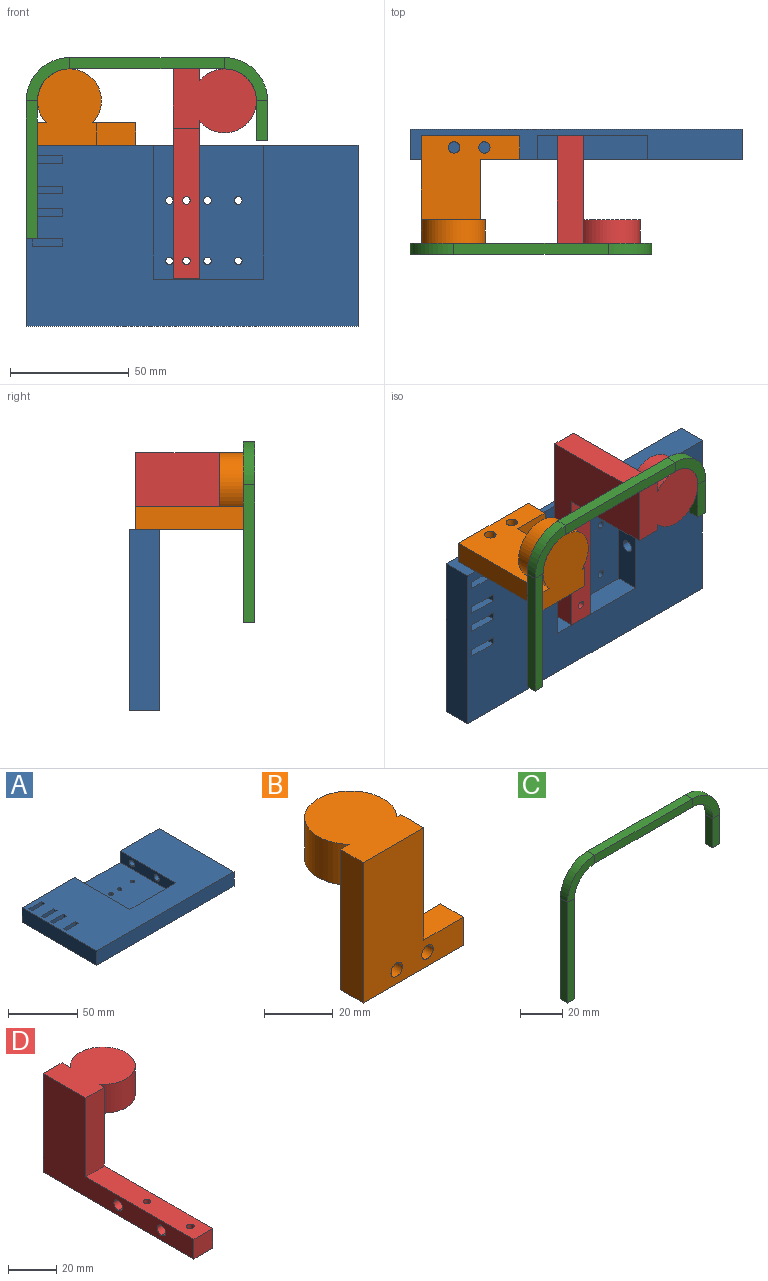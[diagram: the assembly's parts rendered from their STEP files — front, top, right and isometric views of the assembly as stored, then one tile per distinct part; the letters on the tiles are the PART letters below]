
ASSEMBLY  parts=4 mates=9
PART A: 62 faces, bbox 139.7x76.2x12.7 mm
  f0: plane 4.76x4.76mm, normal (0,1,0), area 17.8mm2, adj f1,f2
  f1: cylinder r=2.38mm len=6.35mm, axis (0,1,0), area 47.5mm2, adj f0,f2,f59
  f2: cylinder r=2.38mm len=6.35mm, axis (0,1,0), area 47.5mm2, adj f0,f1,f59
  f3: plane 4.76x4.76mm, normal (0,1,0), area 17.8mm2, adj f4,f5
  f4: cylinder r=2.38mm len=6.35mm, axis (0,1,0), area 47.5mm2, adj f3,f5,f59
  f5: cylinder r=2.38mm len=6.35mm, axis (0,1,0), area 47.5mm2, adj f3,f4,f59
  f6: cylinder r=1.59mm len=3.18mm, axis (0,0,1), area 13.3mm2, adj f7,f58,f61
  f7: cylinder r=1.59mm len=3.18mm, axis (0,0,1), area 13.3mm2, adj f6,f58,f61
  f8: cylinder r=1.59mm len=3.18mm, axis (0,0,1), area 13.3mm2, adj f9,f58,f61
  f9: cylinder r=1.59mm len=3.18mm, axis (0,0,1), area 13.3mm2, adj f8,f58,f61
  f10: cylinder r=1.59mm len=3.18mm, axis (0,0,1), area 13.3mm2, adj f11,f58,f61
  f11: cylinder r=1.59mm len=3.18mm, axis (0,0,1), area 13.3mm2, adj f10,f58,f61
  f12: cylinder r=1.59mm len=3.18mm, axis (0,0,1), area 13.3mm2, adj f13,f58,f61
  f13: cylinder r=1.59mm len=3.18mm, axis (0,0,1), area 13.3mm2, adj f12,f58,f61
  f14: cylinder r=1.59mm len=3.18mm, axis (0,0,1), area 13.3mm2, adj f15,f58,f61
  f15: cylinder r=1.59mm len=3.18mm, axis (0,0,1), area 13.3mm2, adj f14,f58,f61
  f16: cylinder r=1.59mm len=3.18mm, axis (0,0,1), area 13.3mm2, adj f17,f58,f61
  f17: cylinder r=1.59mm len=3.18mm, axis (0,0,1), area 13.3mm2, adj f16,f58,f61
  f18: cylinder r=1.59mm len=3.18mm, axis (0,0,1), area 13.3mm2, adj f19,f58,f61
  f19: cylinder r=1.59mm len=3.18mm, axis (0,0,1), area 13.3mm2, adj f18,f58,f61
  f20: cylinder r=1.59mm len=3.18mm, axis (0,0,1), area 13.3mm2, adj f21,f58,f61
  f21: cylinder r=1.59mm len=3.18mm, axis (0,0,1), area 13.3mm2, adj f20,f58,f61
  f22: plane 12.7x3.23mm, normal (0,0,1), area 41mm2, adj f23,f24,f25,f26
  f23: plane 12.7x10.03mm, normal (0,1,0), area 127.4mm2, adj f22,f24,f26,f56
  f24: plane 10.03x3.23mm, normal (-1,0,0), area 32.4mm2, adj f22,f23,f25,f56
  f25: plane 12.7x10.03mm, normal (0,-1,0), area 127.4mm2, adj f22,f24,f26,f56
  f26: plane 10.03x3.23mm, normal (1,0,0), area 32.4mm2, adj f22,f23,f25,f56
  f27: plane 12.7x3.23mm, normal (0,0,1), area 41mm2, adj f28,f29,f30,f31
  f28: plane 12.7x10.03mm, normal (0,1,0), area 127.4mm2, adj f27,f29,f31,f56
  f29: plane 10.03x3.23mm, normal (-1,0,0), area 32.4mm2, adj f27,f28,f30,f56
  f30: plane 12.7x10.03mm, normal (0,-1,0), area 127.4mm2, adj f27,f29,f31,f56
  f31: plane 10.03x3.23mm, normal (1,0,0), area 32.4mm2, adj f27,f28,f30,f56
  f32: plane 12.7x3.23mm, normal (0,0,1), area 41mm2, adj f33,f34,f35,f36
  f33: plane 12.7x10.03mm, normal (0,1,0), area 127.4mm2, adj f32,f34,f36,f56
  f34: plane 10.03x3.23mm, normal (-1,0,0), area 32.4mm2, adj f32,f33,f35,f56
  f35: plane 12.7x10.03mm, normal (0,-1,0), area 127.4mm2, adj f32,f34,f36,f56
  f36: plane 10.03x3.23mm, normal (1,0,0), area 32.4mm2, adj f32,f33,f35,f56
  f37: plane 12.7x3.23mm, normal (0,0,1), area 41mm2, adj f38,f39,f40,f41
  f38: plane 12.7x10.03mm, normal (0,1,0), area 127.4mm2, adj f37,f39,f41,f56
  f39: plane 10.03x3.23mm, normal (-1,0,0), area 32.4mm2, adj f37,f38,f40,f56
  f40: plane 12.7x10.03mm, normal (0,-1,0), area 127.4mm2, adj f37,f39,f41,f56
  f41: plane 10.03x3.23mm, normal (1,0,0), area 32.4mm2, adj f37,f38,f40,f56
  f42: cylinder r=2.54mm len=39.62mm, axis (1,0,0), area 316.2mm2, adj f43,f47,f57
  f43: cylinder r=2.54mm len=39.62mm, axis (1,0,0), area 316.2mm2, adj f42,f47,f57
  f44: cylinder r=2.54mm len=39.62mm, axis (1,0,0), area 316.2mm2, adj f45,f47,f57
  f45: cylinder r=2.54mm len=39.62mm, axis (1,0,0), area 316.2mm2, adj f44,f47,f57
  f46: plane 139.7x12.7mm, normal (0,-1,0), area 1774.2mm2, adj f47,f56,f60,f61
  f47: plane 76.2x12.7mm, normal (1,0,0), area 927.2mm2, adj f42,f43,f44,f45,f46,f56,f59,f61
  f48: plane 5.08x5.08mm, normal (1,0,0), area 20.3mm2, adj f49,f50
  f49: cylinder r=2.54mm len=15.49mm, axis (1,0,0), area 123.6mm2, adj f48,f50,f55
  f50: cylinder r=2.54mm len=15.49mm, axis (1,0,0), area 123.6mm2, adj f48,f49,f55
  f51: plane 5.08x5.08mm, normal (1,0,0), area 20.3mm2, adj f52,f53
  f52: cylinder r=2.54mm len=15.49mm, axis (1,0,0), area 123.6mm2, adj f51,f53,f55
  f53: cylinder r=2.54mm len=15.49mm, axis (1,0,0), area 123.6mm2, adj f51,f52,f55
  f54: plane 46.48x10.03mm, normal (0,1,0), area 466.4mm2, adj f55,f56,f57,f58
  f55: plane 56.32x10.03mm, normal (1,0,0), area 524.6mm2, adj f49,f50,f52,f53,f54,f56,f58,f59
  f56: plane 139.7x76.2mm, normal (0,0,1), area 7863.2mm2, adj f23,f24,f25,f26,f28,f29,f30,f31
  f57: plane 56.32x10.03mm, normal (-1,0,0), area 524.6mm2, adj f42,f43,f44,f45,f54,f56,f58,f59
  f58: plane 56.32x46.48mm, normal (0,0,1), area 2554.7mm2, adj f6,f7,f8,f9,f10,f11,f12,f13
  f59: plane 139.7x12.7mm, normal (0,1,0), area 1272.2mm2, adj f1,f2,f4,f5,f47,f55,f56,f57
  f60: plane 76.2x12.7mm, normal (-1,0,0), area 967.7mm2, adj f46,f56,f59,f61
  f61: plane 139.7x76.2mm, normal (0,0,-1), area 10581.8mm2, adj f6,f7,f8,f9,f10,f11,f12,f13
PART B: 14 faces, bbox 41.3x32.2x50.1 mm
  f0: cylinder r=2.38mm len=9.46mm, axis (0,-1,0), area 70.8mm2, adj f1,f9,f11
  f1: cylinder r=2.38mm len=9.46mm, axis (0,-1,0), area 70.8mm2, adj f0,f9,f11
  f2: cylinder r=2.38mm len=9.46mm, axis (0,-1,0), area 70.8mm2, adj f3,f9,f11
  f3: cylinder r=2.38mm len=9.46mm, axis (0,-1,0), area 70.8mm2, adj f2,f9,f11
  f4: plane 26.92x22.7mm, normal (0,0,-1), area 512.1mm2, adj f5,f9
  f5: cylinder r=13.46mm len=26.92mm, axis (0,0,1), area 914.9mm2, adj f4,f6,f9
  f6: plane 32.16x26.92mm, normal (0,0,1), area 747.6mm2, adj f5,f7,f9,f10,f11
  f7: plane 40.03x9.46mm, normal (1,0,0), area 378.7mm2, adj f6,f8,f9,f11
  f8: plane 16.36x9.46mm, normal (0,0,1), area 154.8mm2, adj f7,f9,f11,f12
  f9: plane 50.06x41.25mm, normal (0,1,0), area 1088.5mm2, adj f0,f1,f2,f3,f4,f5,f6,f7
  f10: plane 50.06x9.46mm, normal (-1,0,0), area 473.7mm2, adj f6,f9,f11,f13
  f11: plane 50.06x41.25mm, normal (0,-1,0), area 1374.7mm2, adj f0,f1,f2,f3,f6,f7,f8,f10
  f12: plane 10.03x9.46mm, normal (1,0,0), area 94.9mm2, adj f8,f9,f11,f13
  f13: plane 41.25x9.46mm, normal (0,0,-1), area 390.3mm2, adj f9,f10,f11,f12
PART C: 22 faces, bbox 101.6x4.8x76.2 mm
  f0: plane 57.99x4.75mm, normal (0,1,0), area 275.4mm2, adj f2,f3,f4,f19
  f1: plane 57.99x4.75mm, normal (0,-1,0), area 275.4mm2, adj f2,f3,f4,f18
  f2: plane 4.75x4.75mm, normal (0,0,-1), area 22.6mm2, adj f0,f1,f3,f4
  f3: plane 57.99x4.75mm, normal (1,0,0), area 275.4mm2, adj f0,f1,f2,f21
  f4: plane 57.99x4.75mm, normal (-1,0,0), area 275.4mm2, adj f0,f1,f2,f20
  f5: plane 65.18x4.75mm, normal (0,1,0), area 309.6mm2, adj f7,f8,f15,f19
  f6: plane 65.18x4.75mm, normal (0,-1,0), area 309.6mm2, adj f7,f8,f14,f18
  f7: plane 65.18x4.75mm, normal (0,0,-1), area 309.6mm2, adj f5,f6,f17,f21
  f8: plane 65.18x4.75mm, normal (0,0,1), area 309.6mm2, adj f5,f6,f16,f20
  f9: plane 16.84x4.75mm, normal (0,1,0), area 80mm2, adj f10,f12,f13,f15
  f10: plane 4.75x4.75mm, normal (0,0,-1), area 22.6mm2, adj f9,f11,f12,f13
  f11: plane 16.84x4.75mm, normal (0,-1,0), area 80mm2, adj f10,f12,f13,f14
  f12: plane 16.84x4.75mm, normal (-1,0,0), area 80mm2, adj f9,f10,f11,f17
  f13: plane 16.84x4.75mm, normal (1,0,0), area 80mm2, adj f9,f10,f11,f16
  f14: plane 18.21x18.21mm, normal (0,-1,0), area 118.2mm2, adj f6,f11,f16,f17
  f15: plane 18.21x18.21mm, normal (0,1,0), area 118.2mm2, adj f5,f9,f16,f17
  f16: cylinder r=18.21mm len=18.21mm, axis (0,-1,0), area 135.9mm2, adj f8,f13,f14,f15
  f17: cylinder r=13.46mm len=13.46mm, axis (0,-1,0), area 100.4mm2, adj f7,f12,f14,f15
  f18: plane 18.21x18.21mm, normal (0,-1,0), area 118.2mm2, adj f1,f6,f20,f21
  f19: plane 18.21x18.21mm, normal (0,1,0), area 118.2mm2, adj f0,f5,f20,f21
  f20: cylinder r=18.21mm len=18.21mm, axis (0,-1,0), area 135.9mm2, adj f4,f8,f18,f19
  f21: cylinder r=13.46mm len=13.46mm, axis (0,-1,0), area 100.4mm2, adj f3,f7,f18,f19
PART D: 18 faces, bbox 35x88.4x50.1 mm
  f0: cylinder r=2.54mm len=10.99mm, axis (1,0,0), area 87.7mm2, adj f1,f13,f15
  f1: cylinder r=2.54mm len=10.99mm, axis (1,0,0), area 87.7mm2, adj f0,f13,f15
  f2: cylinder r=2.54mm len=10.99mm, axis (1,0,0), area 87.7mm2, adj f3,f13,f15
  f3: cylinder r=2.54mm len=10.99mm, axis (1,0,0), area 87.7mm2, adj f2,f13,f15
  f4: cylinder r=1.59mm len=10.03mm, axis (0,0,1), area 50mm2, adj f5,f8,f17
  f5: cylinder r=1.59mm len=10.03mm, axis (0,0,1), area 50mm2, adj f4,f8,f17
  f6: cylinder r=1.59mm len=10.03mm, axis (0,0,1), area 50mm2, adj f7,f8,f17
  f7: cylinder r=1.59mm len=10.03mm, axis (0,0,1), area 50mm2, adj f6,f8,f17
  f8: plane 63.5x10.99mm, normal (0,0,1), area 681.7mm2, adj f4,f5,f6,f7,f9,f13,f15,f16
  f9: plane 40.03x10.99mm, normal (0,-1,0), area 439.8mm2, adj f8,f10,f13,f15
  f10: plane 34.95x26.92mm, normal (0,0,1), area 808.8mm2, adj f9,f11,f13,f14,f15
  f11: cylinder r=13.46mm len=26.92mm, axis (0,0,1), area 969.6mm2, adj f10,f12,f13
  f12: plane 26.92x23.97mm, normal (0,0,-1), area 535.3mm2, adj f11,f13
  f13: plane 88.39x50.06mm, normal (1,0,0), area 1596.8mm2, adj f0,f1,f2,f3,f8,f9,f10,f11
  f14: plane 50.06x10.99mm, normal (0,1,0), area 550mm2, adj f10,f13,f15,f17
  f15: plane 88.39x50.06mm, normal (-1,0,0), area 1842.7mm2, adj f0,f1,f2,f3,f8,f9,f10,f14
  f16: plane 10.99x10.03mm, normal (0,-1,0), area 110.2mm2, adj f8,f13,f15,f17
  f17: plane 88.39x10.99mm, normal (0,0,-1), area 955.2mm2, adj f4,f5,f6,f7,f13,f14,f15,f16
PLACE A rot(axis=(1,0,0),90deg) t=(2.03,70.57,-53.85)mm
PLACE B rot(axis=(1,0,0),90deg) t=(2.03,70.57,-53.85)mm
PLACE C rot(axis=(-1,0,0),0deg) t=(1.89,35.29,-16.96)mm
PLACE D rot(axis=(1,0,0),90deg) t=(63.8,80.61,-33.9)mm
MATE slider B.f0 <-> A.f1  axis (0,0,-1) through (33.09,75.59,27.08)mm
MATE planar C.f6 <-> B.f6  axis (0,-1,0) through (52.69,30.54,56.87)mm
MATE slider D.f0 <-> A.f44  axis (1,0,0) through (74.79,75.59,10.55)mm
MATE planar B.f11 <-> A.f59  axis (0,0,-1) through (21.35,57.45,22.35)mm
MATE slider B.f2 <-> A.f4  axis (0,0,-1) through (20.39,75.59,22.35)mm
MATE slider D.f2 <-> A.f42  axis (1,0,0) through (69.29,75.59,-14.85)mm
MATE parallel C.f2 <-> B.f11  axis (0,0,-1) through (4.27,32.92,-16.96)mm
MATE planar C.f3 <-> B.f10  axis (1,0,0) through (6.64,32.92,12.03)mm
MATE planar D.f14 <-> C.f7  axis (0,0,1) through (69.29,55.57,54.49)mm
